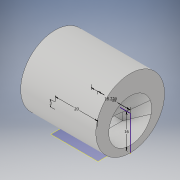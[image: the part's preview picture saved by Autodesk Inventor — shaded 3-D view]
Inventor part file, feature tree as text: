
AUTODESK INVENTOR PART (.ipt)
format: ipt  version: 2019 (Build 230136000, 136)  size: 232,448 bytes
history: native  units: in
note: dims shown in document units (in); Inventor stores cm internally (conversion verified against a paired STEP export)
features: sketch x7, extrude x2, revolve x1, loft x1, fillet x1, plane x1, other x1
ambient origin geometry x8: Origin, YZ Plane, XZ Plane, XY Plane, X Axis, Y Axis, Z Axis, Center Point
bodies: Solid1 (feature_tree)
feature tree (14):
  revolve  "Revolution1"  [1 undecoded]
  sketch  "Sketch2"  dims[d3=0.5906in d4=90.0deg]
  extrude  "Extrusion1"  TaperAngle=90.0deg  [1 undecoded]
  sketch  "Sketch4"  dims[d9=0.7874in d10=0.0in d11=90.0deg]
  sketch  "Sketch5"  dims[d12=0.0in d13=90.0deg]
  loft  "Loft1"
  fillet  "Fillet1"  Radius=0.1969in
  sketch  "Sketch6"  dims[d14=0.2362in]
  plane  "Work Plane1"
  extrude  "Extrusion2"  TaperAngle=0.0deg  [1 undecoded]
  sketch  "Sketch1"  dims[d0=0.1181in d1=0.7874in]
  sketch  "Sketch3"  dims[d5=0.1181in d6=0.5118in d7=0.1969in d8=0.0in]
  other  "Edges1"
  sketch  "Sketch7"  dims[d15=0.5118in d16=0.1969in d17=0.0in d18=0.6299in d19=0.7177in]
note: 3 required parameter values undecoded (feature->parameter linkage not recoverable at this tier; creation-order binding heuristic only, values carry confidence <= 0.55)